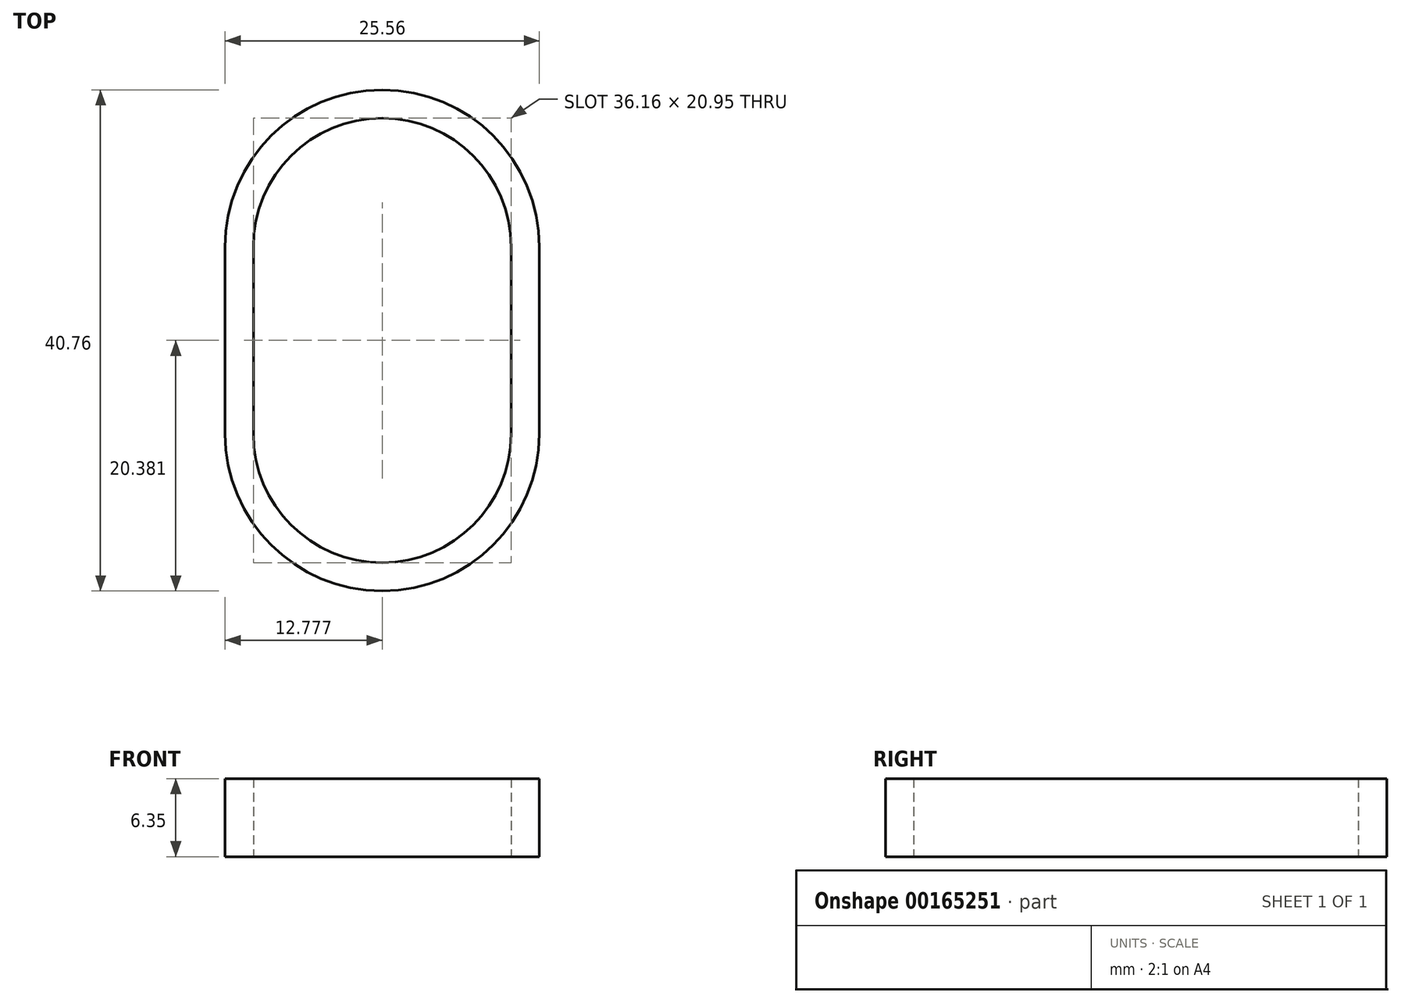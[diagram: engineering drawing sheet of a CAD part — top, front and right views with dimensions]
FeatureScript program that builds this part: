
annotation { "Feature Type Name" : "Feature", "Feature Type Description" : "" }
export const myFeature = defineFeature(function(context is Context, id is Id, definition is map)
    precondition{}
    {
        {
            var Q0;
            Q0=qCreatedBy(makeId("Top.planeOp"),FACE);
            var sketch = newSketch(context, id + "F0", { "sketchPlane" : qUnion([Q0])});
            skLineSegment(sketch, "E0.bottom", {"start": v(0, 0) * mm, "end": v(20.96, 0) * mm, "construction": true});
            skLineSegment(sketch, "E0.top", {"start": v(0, 15.2) * mm, "end": v(20.96, 15.2) * mm, "construction": true});
            skLineSegment(sketch, "E0.left", {"start": v(0, 0) * mm, "end": v(0, 15.2) * mm});
            skLineSegment(sketch, "E0.right", {"start": v(20.96, 0) * mm, "end": v(20.96, 15.2) * mm});
            skArc(sketch, "E1", {"start": v(20.96, 15.2) * mm, "mid": v(10.48, 25.68) * mm, "end": v(0, 15.2) * mm});
            skArc(sketch, "E2", {"start": v(0, 0) * mm, "mid": v(10.48, -10.48) * mm, "end": v(20.96, 0) * mm});
            skLineSegment(sketch, "E3", {"start": v(0, 15.2) * mm, "end": v(-2.3, 15.2) * mm, "construction": true});
            skLineSegment(sketch, "E4", {"start": v(20.96, 15.2) * mm, "end": v(23.25, 15.2) * mm, "construction": true});
            skLineSegment(sketch, "E5", {"start": v(23.26, 15.2) * mm, "end": v(23.26, 0) * mm});
            skLineSegment(sketch, "E6", {"start": v(23.25, 0) * mm, "end": v(20.96, 0) * mm, "construction": true});
            skLineSegment(sketch, "E7", {"start": v(0, 0) * mm, "end": v(-2.3, 0) * mm});
            skLineSegment(sketch, "E8", {"start": v(-2.3, 0) * mm, "end": v(-2.3, 15.2) * mm});
            skArc(sketch, "E9", {"start": v(-2.3, 0) * mm, "mid": v(10.48, -12.78) * mm, "end": v(23.26, 0) * mm});
            skArc(sketch, "E10", {"start": v(23.25, 15.2) * mm, "mid": v(10.48, 27.98) * mm, "end": v(-2.3, 15.2) * mm});
            skSolve(sketch);
        }
        {
            var Q0;
            Q0=qSketchRegion(id+"F0",true);
            extrude(context, id + "F1", {"entities" : qUnion([Q0]), "depth" : 6.35 * mm});
        }
    });
